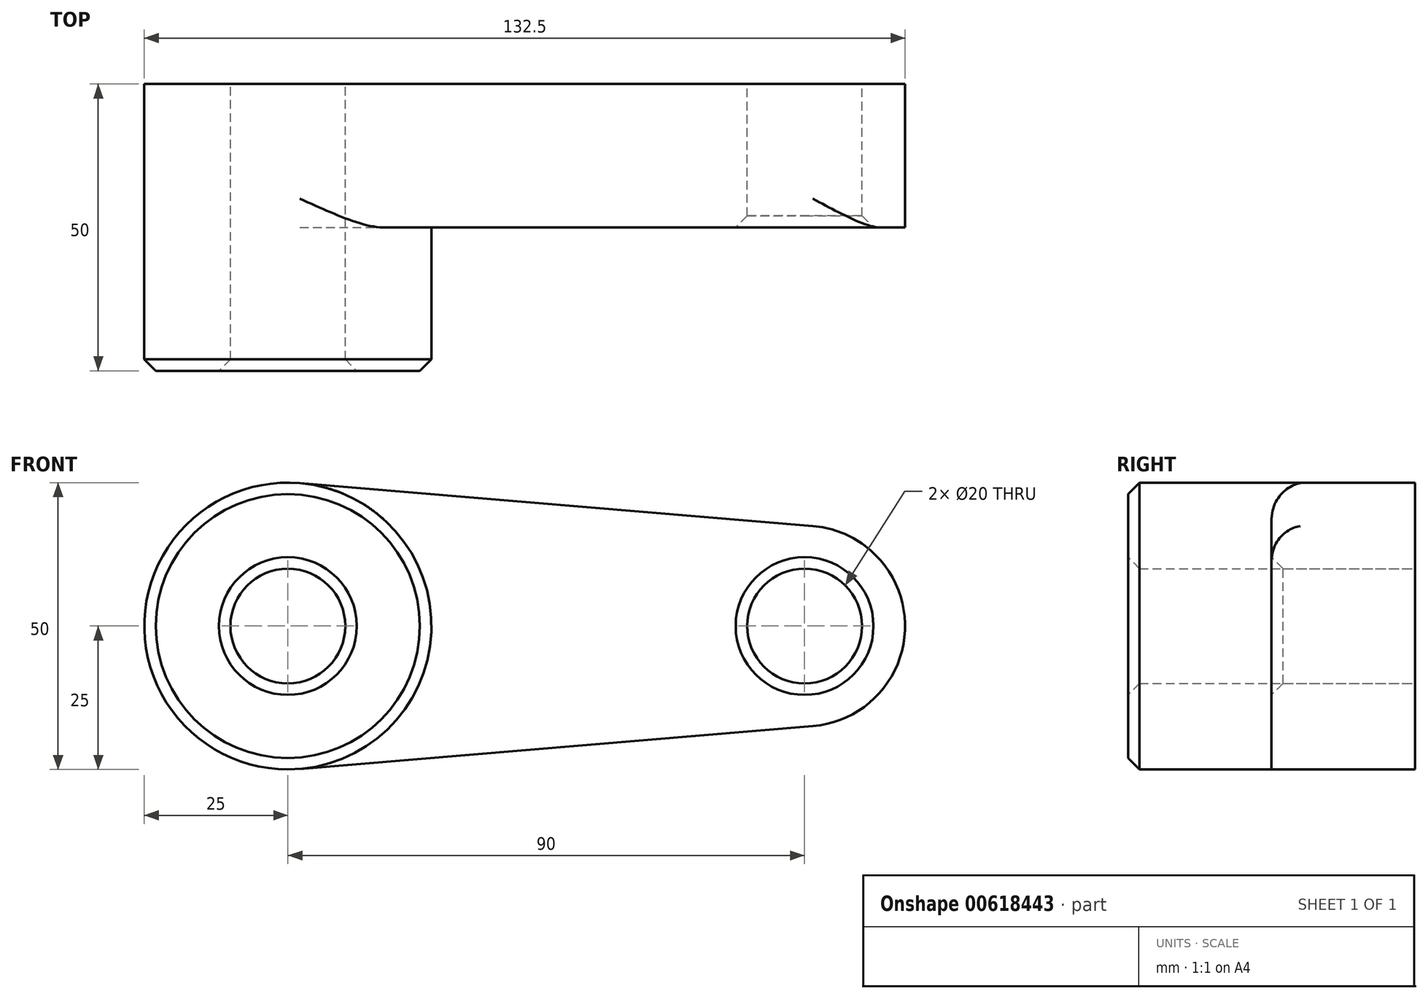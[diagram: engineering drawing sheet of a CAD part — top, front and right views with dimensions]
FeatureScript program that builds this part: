
annotation { "Feature Type Name" : "Feature", "Feature Type Description" : "" }
export const myFeature = defineFeature(function(context is Context, id is Id, definition is map)
    precondition{}
    {
        {
            var Q0;
            Q0=qCreatedBy(makeId("Front.planeOp"),FACE);
            var sketch = newSketch(context, id + "F0", { "sketchPlane" : qUnion([Q0])});
            skCircle(sketch, "E0", {"center": v(0, 0) * mm, "radius": 25 * mm});
            skCircle(sketch, "E1", {"center": v(90, 0) * mm, "radius": 17.5 * mm});
            skLineSegment(sketch, "E2", {"start": v(2.08, 24.91) * mm, "end": v(91.46, 17.44) * mm});
            skLineSegment(sketch, "E3", {"start": v(2.08, -24.91) * mm, "end": v(91.46, -17.44) * mm});
            skCircle(sketch, "E4", {"center": v(0, 0) * mm, "radius": 10 * mm});
            skCircle(sketch, "E5", {"center": v(90, 0) * mm, "radius": 10 * mm});
            skSolve(sketch);
        }
        {
            var Q0;
            Q0=qSketchRegion(id+"F0",true);
            extrude(context, id + "F1", {"entities" : qUnion([Q0]), "depth" : 25 * mm});
        }
        {
            var Q0;
            Q0=makeQuery(id+"F0.imprint","IMPRINT",FACE,{"disambiguationData":[TD([[makeQuery(id+"F0.imprint","IMPRINT",EDGE,{"derivedFrom":sQuery(id+"F0.wireOp",EDGE,"E4")}),-1.0]])]});
            extrude(context, id + "F2", {"entities" : qUnion([Q0]), "operationType" : NewBodyOperationType.ADD, "depth" : 50 * mm});
        }
        {
            var Q0;
            Q0=makeQuery(id+"F2.opExtrude","CAP_EDGE",EDGE,{"disambiguationData":[OSD([sQuery(id+"F0.wireOp",EDGE,"E0")])],"isStart":false});
            var Q1;
            Q1=makeQuery(id+"F2.opExtrude","CAP_EDGE",EDGE,{"disambiguationData":[OSD([sQuery(id+"F0.wireOp",EDGE,"E4")])],"isStart":false});
            var Q2;
            Q2=makeQuery(id+"F1.opExtrude","CAP_EDGE",EDGE,{"disambiguationData":[OSD([sQuery(id+"F0.wireOp",EDGE,"E5")])],"isStart":false});
            chamfer(context, id + "F3", {"entities" : qUnion([Q0, Q1, Q2]), "width" : 2 * mm, "tangentPropagation" : true});
        }
        {
            var Q0;
            Q0=makeQuery(id+"F1.opExtrude","CAP_EDGE",EDGE,{"disambiguationData":[OSD([sQuery(id+"F0.wireOp",EDGE,"E2")])],"isStart":false});
            fillet(context, id + "F4", {"entities" : qUnion([Q0]), "radius" : 5 * mm, "allowEdgeOverflow" : false});
        }
    });
